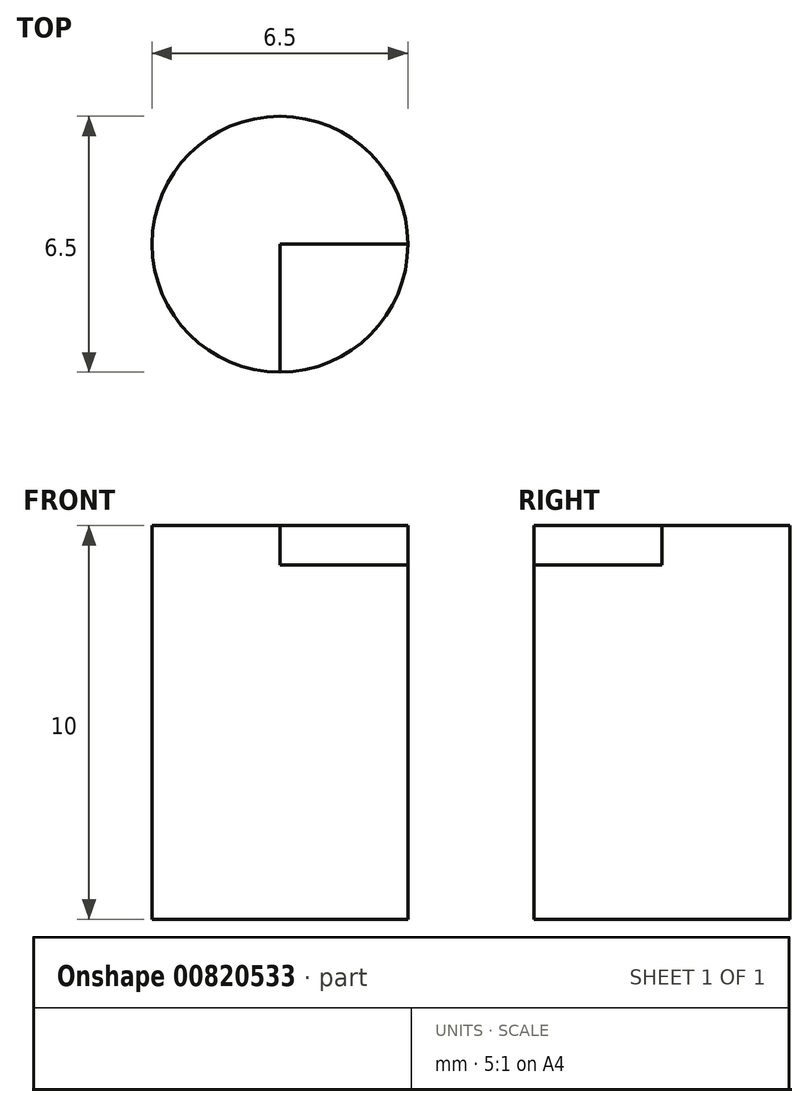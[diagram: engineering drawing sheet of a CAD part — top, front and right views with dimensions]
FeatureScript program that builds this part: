
annotation { "Feature Type Name" : "Feature", "Feature Type Description" : "" }
export const myFeature = defineFeature(function(context is Context, id is Id, definition is map)
    precondition{}
    {
        {
            var Q0;
            Q0=qCreatedBy(makeId("Top.planeOp"),FACE);
            var sketch = newSketch(context, id + "F0", { "sketchPlane" : qUnion([Q0])});
            skCircle(sketch, "E0", {"center": v(0, 0) * mm, "radius": 3.25 * mm});
            skSolve(sketch);
        }
        {
            var Q0;
            Q0=makeQuery(id+"F0.imprint","IMPRINT",FACE,{"disambiguationData":[TD([[makeQuery(id+"F0.imprint","IMPRINT",EDGE,{"derivedFrom":sQuery(id+"F0.wireOp",EDGE,"E0")}),1.0]])]});
            extrude(context, id + "F1", {"entities" : qUnion([Q0]), "depth" : 10 * mm, "offsetDistance" : 25 * mm});
        }
        {
            var Q0;
            Q0=makeQuery(id+"F1.opExtrude","CAP_FACE",FACE,{"disambiguationData":[OSD([sQuery(id+"F0.wireOp",EDGE,"E0")])],"isStart":false});
            var sketch = newSketch(context, id + "F2", { "sketchPlane" : qUnion([Q0])});
            skLineSegment(sketch, "E1.bottom", {"start": v(0, 0) * mm, "end": v(6.38, 0) * mm});
            skLineSegment(sketch, "E1.top", {"start": v(0, -5.63) * mm, "end": v(6.38, -5.63) * mm});
            skLineSegment(sketch, "E1.left", {"start": v(0, 0) * mm, "end": v(0, -5.63) * mm});
            skLineSegment(sketch, "E1.right", {"start": v(6.38, 0) * mm, "end": v(6.38, -5.63) * mm});
            skSolve(sketch);
        }
        {
            var Q0;
            {var subQ2=sQuery(id+"F2.wireOp",EDGE,"E1.top");Q0=makeQuery(id+"F2.imprint","IMPRINT",FACE,{"disambiguationData":[TD([[makeQuery(id+"F2.imprint","IMPRINT",EDGE,{"derivedFrom":subQ2}),1.0]])]});}
            var Q1;
            {var subQ0=sQuery(id+"F2.wireOp",EDGE,"E1.left");var subQ1=sQuery(id+"F2.wireOp",EDGE,"E1.bottom");var subQ2=makeQuery(id+"F2.imprint","INTERSECT",VERTEX,{"derivedFrom":[subQ1,subQ0]});Q1=makeQuery(id+"F2.imprint","IMPRINT",FACE,{"disambiguationData":[TD([[makeQuery(id+"F2.imprint","IMPRINT",EDGE,{"disambiguationData":[TD([[subQ2,-1.0]])],"derivedFrom":subQ1}),-1.0]])]});}
            extrude(context, id + "F3", {"entities" : qUnion([Q0, Q1]), "operationType" : NewBodyOperationType.REMOVE, "oppositeDirection" : true, "depth" : 1 * mm, "offsetDistance" : 25 * mm});
        }
        {
            var Q0;
            Q0=makeQuery(id+"F1.opExtrude","SWEPT_BODY",BODY,{"disambiguationData":[OSD([sQuery(id+"F0.wireOp",EDGE,"E0")])]});
            transform(context, id + "F4", {"entities" : qUnion([Q0]), "transformType" : TransformType.TRANSLATION_3D, "dx" : 0 * mm, "dy" : 0 * mm, "dz" : 0 * mm, "makeCopy" : true});
        }
        {
            var Q0;
            Q0=makeQuery(id+"F4.opPattern","COPY",BODY,{"derivedFrom":makeQuery(id+"F1.opExtrude","SWEPT_BODY",BODY,{"disambiguationData":[OSD([sQuery(id+"F0.wireOp",EDGE,"E0")])]}),"instanceName":"1"});
            transform(context, id + "F5", {"entities" : qUnion([Q0]), "transformType" : TransformType.TRANSLATION_3D, "dx" : 0 * mm, "dy" : 0 * mm, "dz" : 0 * mm, "makeCopy" : true});
        }
        {
            var Q0;
            Q0=makeQuery(id+"F5.opPattern","COPY",BODY,{"derivedFrom":makeQuery(id+"F4.opPattern","COPY",BODY,{"derivedFrom":makeQuery(id+"F1.opExtrude","SWEPT_BODY",BODY,{"disambiguationData":[OSD([sQuery(id+"F0.wireOp",EDGE,"E0")])]}),"instanceName":"1"}),"instanceName":"1"});
            transform(context, id + "F6", {"entities" : qUnion([Q0]), "transformType" : TransformType.TRANSLATION_3D, "dx" : 0 * mm, "dy" : 0 * mm, "dz" : 0 * mm, "makeCopy" : true});
        }
        {
            var Q0;
            Q0=makeQuery(id+"F6.opPattern","COPY",BODY,{"derivedFrom":makeQuery(id+"F5.opPattern","COPY",BODY,{"derivedFrom":makeQuery(id+"F4.opPattern","COPY",BODY,{"derivedFrom":makeQuery(id+"F1.opExtrude","SWEPT_BODY",BODY,{"disambiguationData":[OSD([sQuery(id+"F0.wireOp",EDGE,"E0")])]}),"instanceName":"1"}),"instanceName":"1"}),"instanceName":"1"});
            transform(context, id + "F7", {"entities" : qUnion([Q0]), "transformType" : TransformType.TRANSLATION_3D, "dx" : 0 * mm, "dy" : 0 * mm, "dz" : 0 * mm, "makeCopy" : true});
        }
        {
            var Q0;
            Q0=makeQuery(id+"F7.opPattern","COPY",BODY,{"derivedFrom":makeQuery(id+"F6.opPattern","COPY",BODY,{"derivedFrom":makeQuery(id+"F5.opPattern","COPY",BODY,{"derivedFrom":makeQuery(id+"F4.opPattern","COPY",BODY,{"derivedFrom":makeQuery(id+"F1.opExtrude","SWEPT_BODY",BODY,{"disambiguationData":[OSD([sQuery(id+"F0.wireOp",EDGE,"E0")])]}),"instanceName":"1"}),"instanceName":"1"}),"instanceName":"1"}),"instanceName":"1"});
            transform(context, id + "F8", {"entities" : qUnion([Q0]), "transformType" : TransformType.TRANSLATION_3D, "dx" : 0 * mm, "dy" : 0 * mm, "dz" : 0 * mm, "makeCopy" : true});
        }
        {
            var Q0;
            Q0=makeQuery(id+"F8.opPattern","COPY",BODY,{"derivedFrom":makeQuery(id+"F7.opPattern","COPY",BODY,{"derivedFrom":makeQuery(id+"F6.opPattern","COPY",BODY,{"derivedFrom":makeQuery(id+"F5.opPattern","COPY",BODY,{"derivedFrom":makeQuery(id+"F4.opPattern","COPY",BODY,{"derivedFrom":makeQuery(id+"F1.opExtrude","SWEPT_BODY",BODY,{"disambiguationData":[OSD([sQuery(id+"F0.wireOp",EDGE,"E0")])]}),"instanceName":"1"}),"instanceName":"1"}),"instanceName":"1"}),"instanceName":"1"}),"instanceName":"1"});
            transform(context, id + "F9", {"entities" : qUnion([Q0]), "transformType" : TransformType.TRANSLATION_3D, "dx" : 0 * mm, "dy" : 0 * mm, "dz" : 0 * mm, "makeCopy" : true});
        }
        {
            var Q0;
            Q0=makeQuery(id+"F9.opPattern","COPY",BODY,{"derivedFrom":makeQuery(id+"F8.opPattern","COPY",BODY,{"derivedFrom":makeQuery(id+"F7.opPattern","COPY",BODY,{"derivedFrom":makeQuery(id+"F6.opPattern","COPY",BODY,{"derivedFrom":makeQuery(id+"F5.opPattern","COPY",BODY,{"derivedFrom":makeQuery(id+"F4.opPattern","COPY",BODY,{"derivedFrom":makeQuery(id+"F1.opExtrude","SWEPT_BODY",BODY,{"disambiguationData":[OSD([sQuery(id+"F0.wireOp",EDGE,"E0")])]}),"instanceName":"1"}),"instanceName":"1"}),"instanceName":"1"}),"instanceName":"1"}),"instanceName":"1"}),"instanceName":"1"});
            transform(context, id + "F10", {"entities" : qUnion([Q0]), "transformType" : TransformType.TRANSLATION_3D, "dx" : 0 * mm, "dy" : 0 * mm, "dz" : 0 * mm, "makeCopy" : true});
        }
        {
            var Q0;
            Q0=makeQuery(id+"F1.opExtrude","SWEPT_BODY",BODY,{"disambiguationData":[OSD([sQuery(id+"F0.wireOp",EDGE,"E0")])]});
            transform(context, id + "F11", {"entities" : qUnion([Q0]), "transformType" : TransformType.TRANSLATION_3D, "dx" : 0 * mm, "dy" : 0 * mm, "dz" : 0 * mm, "makeCopy" : true});
        }
        {
            var Q0;
            Q0=makeQuery(id+"F4.opPattern","COPY",BODY,{"derivedFrom":makeQuery(id+"F1.opExtrude","SWEPT_BODY",BODY,{"disambiguationData":[OSD([sQuery(id+"F0.wireOp",EDGE,"E0")])]}),"instanceName":"1"});
            var Q1;
            Q1=makeQuery(id+"F5.opPattern","COPY",BODY,{"derivedFrom":makeQuery(id+"F4.opPattern","COPY",BODY,{"derivedFrom":makeQuery(id+"F1.opExtrude","SWEPT_BODY",BODY,{"disambiguationData":[OSD([sQuery(id+"F0.wireOp",EDGE,"E0")])]}),"instanceName":"1"}),"instanceName":"1"});
            var Q2;
            Q2=makeQuery(id+"F6.opPattern","COPY",BODY,{"derivedFrom":makeQuery(id+"F5.opPattern","COPY",BODY,{"derivedFrom":makeQuery(id+"F4.opPattern","COPY",BODY,{"derivedFrom":makeQuery(id+"F1.opExtrude","SWEPT_BODY",BODY,{"disambiguationData":[OSD([sQuery(id+"F0.wireOp",EDGE,"E0")])]}),"instanceName":"1"}),"instanceName":"1"}),"instanceName":"1"});
            var Q3;
            Q3=makeQuery(id+"F7.opPattern","COPY",BODY,{"derivedFrom":makeQuery(id+"F6.opPattern","COPY",BODY,{"derivedFrom":makeQuery(id+"F5.opPattern","COPY",BODY,{"derivedFrom":makeQuery(id+"F4.opPattern","COPY",BODY,{"derivedFrom":makeQuery(id+"F1.opExtrude","SWEPT_BODY",BODY,{"disambiguationData":[OSD([sQuery(id+"F0.wireOp",EDGE,"E0")])]}),"instanceName":"1"}),"instanceName":"1"}),"instanceName":"1"}),"instanceName":"1"});
            var Q4;
            Q4=makeQuery(id+"F8.opPattern","COPY",BODY,{"derivedFrom":makeQuery(id+"F7.opPattern","COPY",BODY,{"derivedFrom":makeQuery(id+"F6.opPattern","COPY",BODY,{"derivedFrom":makeQuery(id+"F5.opPattern","COPY",BODY,{"derivedFrom":makeQuery(id+"F4.opPattern","COPY",BODY,{"derivedFrom":makeQuery(id+"F1.opExtrude","SWEPT_BODY",BODY,{"disambiguationData":[OSD([sQuery(id+"F0.wireOp",EDGE,"E0")])]}),"instanceName":"1"}),"instanceName":"1"}),"instanceName":"1"}),"instanceName":"1"}),"instanceName":"1"});
            var Q5;
            Q5=makeQuery(id+"F9.opPattern","COPY",BODY,{"derivedFrom":makeQuery(id+"F8.opPattern","COPY",BODY,{"derivedFrom":makeQuery(id+"F7.opPattern","COPY",BODY,{"derivedFrom":makeQuery(id+"F6.opPattern","COPY",BODY,{"derivedFrom":makeQuery(id+"F5.opPattern","COPY",BODY,{"derivedFrom":makeQuery(id+"F4.opPattern","COPY",BODY,{"derivedFrom":makeQuery(id+"F1.opExtrude","SWEPT_BODY",BODY,{"disambiguationData":[OSD([sQuery(id+"F0.wireOp",EDGE,"E0")])]}),"instanceName":"1"}),"instanceName":"1"}),"instanceName":"1"}),"instanceName":"1"}),"instanceName":"1"}),"instanceName":"1"});
            var Q6;
            Q6=makeQuery(id+"F10.opPattern","COPY",BODY,{"derivedFrom":makeQuery(id+"F9.opPattern","COPY",BODY,{"derivedFrom":makeQuery(id+"F8.opPattern","COPY",BODY,{"derivedFrom":makeQuery(id+"F7.opPattern","COPY",BODY,{"derivedFrom":makeQuery(id+"F6.opPattern","COPY",BODY,{"derivedFrom":makeQuery(id+"F5.opPattern","COPY",BODY,{"derivedFrom":makeQuery(id+"F4.opPattern","COPY",BODY,{"derivedFrom":makeQuery(id+"F1.opExtrude","SWEPT_BODY",BODY,{"disambiguationData":[OSD([sQuery(id+"F0.wireOp",EDGE,"E0")])]}),"instanceName":"1"}),"instanceName":"1"}),"instanceName":"1"}),"instanceName":"1"}),"instanceName":"1"}),"instanceName":"1"}),"instanceName":"1"});
            var Q7;
            Q7=makeQuery(id+"F11.opPattern","COPY",BODY,{"derivedFrom":makeQuery(id+"F1.opExtrude","SWEPT_BODY",BODY,{"disambiguationData":[OSD([sQuery(id+"F0.wireOp",EDGE,"E0")])]}),"instanceName":"1"});
            deleteBodies(context, id + "F12", {"entities" : qUnion([Q0, Q1, Q2, Q3, Q4, Q5, Q6, Q7])});
        }
    });
